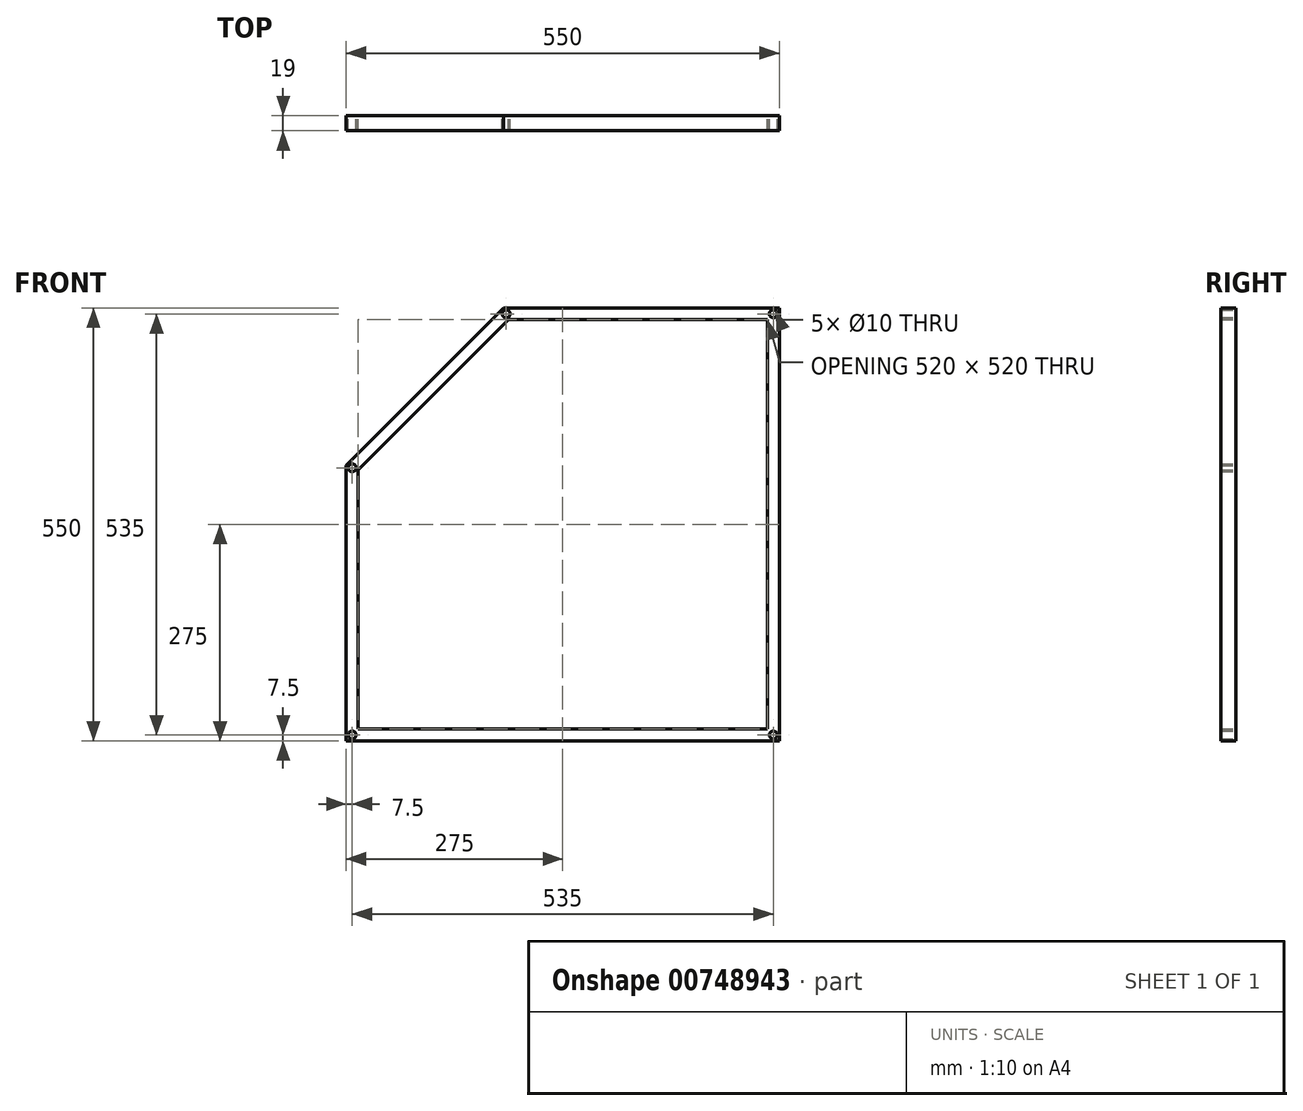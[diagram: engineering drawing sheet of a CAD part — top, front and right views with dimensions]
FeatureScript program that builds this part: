
annotation { "Feature Type Name" : "Feature", "Feature Type Description" : "" }
export const myFeature = defineFeature(function(context is Context, id is Id, definition is map)
    precondition{}
    {
        {
            var Q0;
            Q0=qCreatedBy(makeId("Front.planeOp"),FACE);
            var sketch = newSketch(context, id + "F0", { "sketchPlane" : qUnion([Q0])});
            skLineSegment(sketch, "E0.top", {"start": v(-275, -275) * mm, "end": v(275, -275) * mm});
            skLineSegment(sketch, "E0.right", {"start": v(275, 275) * mm, "end": v(275, -275) * mm});
            skPoint(sketch, "E0.middle", {"position": v(0, 0) * mm});
            skLineSegment(sketch, "E1", {"start": v(-75, 275) * mm, "end": v(275, 275) * mm});
            skLineSegment(sketch, "E2", {"start": v(-275, -275) * mm, "end": v(-275, 75) * mm});
            skLineSegment(sketch, "E3", {"start": v(275, 275) * mm, "end": v(-75, 275) * mm});
            skLineSegment(sketch, "E4", {"start": v(-75, 275) * mm, "end": v(-275, 75) * mm});
            skPoint(sketch, "E5.orphan", {"position": v(-275, 275) * mm});
            skLineSegment(sketch, "E6.0", {"start": v(-260, -260) * mm, "end": v(-260, 68.79) * mm});
            skLineSegment(sketch, "E6.1", {"start": v(-68.79, 260) * mm, "end": v(-260, 68.79) * mm});
            skLineSegment(sketch, "E6.2", {"start": v(-260, -260) * mm, "end": v(260, -260) * mm});
            skLineSegment(sketch, "E6.3", {"start": v(260, 260) * mm, "end": v(260, -260) * mm});
            skLineSegment(sketch, "E6.4", {"start": v(260, 260) * mm, "end": v(-68.79, 260) * mm});
            skLineSegment(sketch, "E7", {"start": v(260, 260) * mm, "end": v(260, -35) * mm});
            skLineSegment(sketch, "E8", {"start": v(-275, 275) * mm, "end": v(-175, 175) * mm, "construction": true});
            skCircle(sketch, "E9", {"center": v(-267.5, 71.9) * mm, "radius": 5 * mm});
            skCircle(sketch, "E10", {"center": v(-267.5, -267.5) * mm, "radius": 5 * mm});
            skCircle(sketch, "E11", {"center": v(267.5, -267.5) * mm, "radius": 5 * mm});
            skCircle(sketch, "E12.MirrorC", {"center": v(-71.9, 267.5) * mm, "radius": 5 * mm});
            skCircle(sketch, "E13.MirrorC", {"center": v(267.5, 267.5) * mm, "radius": 5 * mm});
            skLineSegment(sketch, "E14.trimOffspring", {"start": v(275, -275) * mm, "end": v(391.98, -391.98) * mm, "construction": true});
            skLineSegment(sketch, "E15", {"start": v(47.8, -47.8) * mm, "end": v(-164.4, -260) * mm, "construction": true});
            skLineSegment(sketch, "E16", {"start": v(47.8, -47.8) * mm, "end": v(260, 164.4) * mm, "construction": true});
            skLineSegment(sketch, "E17", {"start": v(260, -260) * mm, "end": v(47.8, -47.8) * mm, "construction": true});
            skLineSegment(sketch, "E18", {"start": v(-164.4, 164.4) * mm, "end": v(47.8, -47.8) * mm, "construction": true});
            skCircle(sketch, "E19", {"center": v(153.9, -153.9) * mm, "radius": 65 * mm, "construction": true});
            skCircle(sketch, "E20", {"center": v(-58.3, 58.3) * mm, "radius": 65 * mm, "construction": true});
            skLineSegment(sketch, "E21", {"start": v(260, 130) * mm, "end": v(-35, 130) * mm});
            skLineSegment(sketch, "E22", {"start": v(-35, 130) * mm, "end": v(-35, 260) * mm});
            skSolve(sketch);
        }
        {
            var Q0;
            Q0=qSketchRegion(id+"F0",true);
            extrude(context, id + "F1", {"entities" : qUnion([Q0]), "depth" : 19 * mm, "offsetDistance" : 25 * mm, "symmetric" : true});
        }
    });
